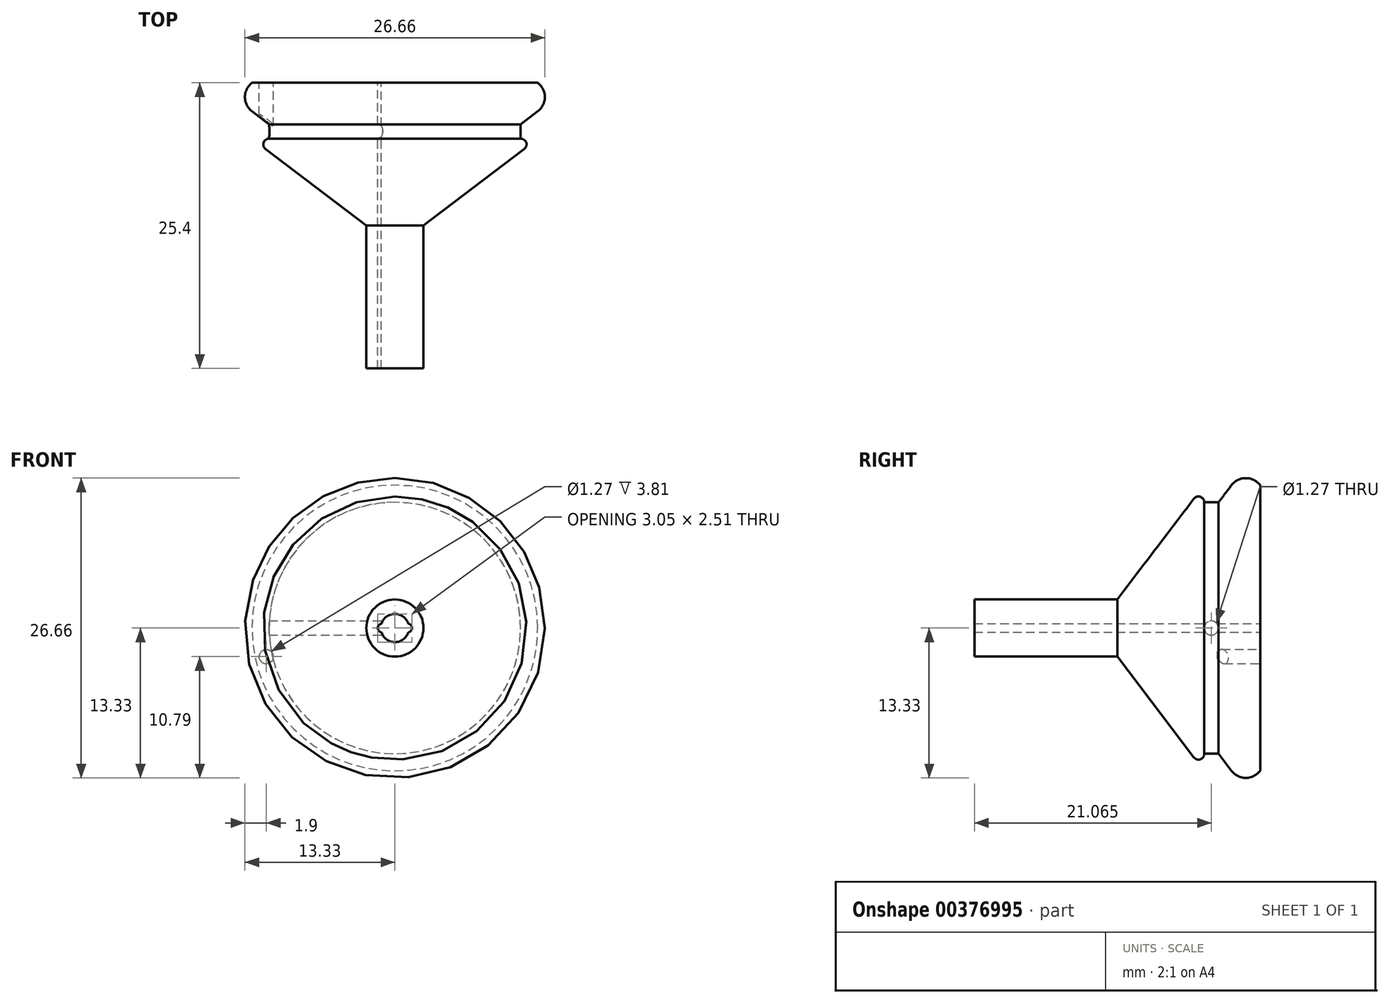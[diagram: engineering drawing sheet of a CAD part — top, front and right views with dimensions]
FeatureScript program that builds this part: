
annotation { "Feature Type Name" : "Feature", "Feature Type Description" : "" }
export const myFeature = defineFeature(function(context is Context, id is Id, definition is map)
    precondition{}
    {
        {
            var Q0;
            Q0=qCreatedBy(makeId("Right.planeOp"),FACE);
            var sketch = newSketch(context, id + "F0", { "sketchPlane" : qUnion([Q0])});
            skLineSegment(sketch, "E0", {"start": v(0, 1) * mm, "end": v(-25.4, 1) * mm});
            skLineSegment(sketch, "E1", {"start": v(-25.4, 1) * mm, "end": v(-25.4, 2.54) * mm});
            skLineSegment(sketch, "E2", {"start": v(-25.4, 2.54) * mm, "end": v(-12.7, 2.54) * mm});
            skLineSegment(sketch, "E3", {"start": v(-2.54, 12.7) * mm, "end": v(0, 12.7) * mm, "construction": true});
            skLineSegment(sketch, "E4", {"start": v(0, 12.7) * mm, "end": v(0, 1) * mm});
            skArc(sketch, "E5", {"start": v(0, 12.7) * mm, "mid": v(-1.27, 13.33) * mm, "end": v(-2.54, 12.7) * mm});
            skLineSegment(sketch, "E6", {"start": v(0, 0) * mm, "end": v(-25.4, 0) * mm, "construction": true});
            skLineSegment(sketch, "E7", {"start": v(-25.4, 0) * mm, "end": v(-25.4, 1) * mm, "construction": true});
            skLineSegment(sketch, "E8", {"start": v(-2.54, 12.7) * mm, "end": v(-3.7, 11.18) * mm});
            skLineSegment(sketch, "E9", {"start": v(-3.7, 11.18) * mm, "end": v(-4.97, 11.18) * mm});
            skLineSegment(sketch, "E10", {"start": v(-4.97, 11.18) * mm, "end": v(-4.97, 12.7) * mm});
            skLineSegment(sketch, "E11", {"start": v(-4.97, 12.7) * mm, "end": v(-12.7, 2.54) * mm});
            skLineSegment(sketch, "E12", {"start": v(-2.54, 12.7) * mm, "end": v(-4.97, 12.7) * mm, "construction": true});
            skSolve(sketch);
        }
        {
            var Q0;
            Q0 = qSketchRegion(id + "F0", true);
            var Q1;
            Q1=sQuery(id+"F0.wireOp",EDGE,"E6");
            revolve(context, id + "F1", {"entities" : qUnion([Q0]), "axis" : qUnion([Q1]), "revolveType" : RevolveType.FULL});
        }
        {
            var Q0;
            Q0=makeQuery(id+"F1.opRevolve","SWEPT_EDGE",EDGE,{"disambiguationData":[OSD([sQuery(id+"F0.wireOp",EDGE,"E10"),sQuery(id+"F0.wireOp",EDGE,"E11")])]});
            fillet(context, id + "F2", {"entities" : qUnion([Q0]), "radius" : 0.5 * mm, "tangentPropagation" : true, "allowEdgeOverflow" : false});
        }
        {
            var Q0;
            Q0=makeQuery(id+"F1.opRevolve","SWEPT_FACE",FACE,{"disambiguationData":[OSD([sQuery(id+"F0.wireOp",EDGE,"E4")])]});
            var sketch = newSketch(context, id + "F3", { "sketchPlane" : qUnion([Q0])});
            skLineSegment(sketch, "E13.bottom", {"start": v(-1.14, -0.13) * mm, "end": v(1.14, -0.13) * mm});
            skLineSegment(sketch, "E13.top", {"start": v(-1.14, 0.13) * mm, "end": v(1.14, 0.13) * mm});
            skLineSegment(sketch, "E13.left", {"start": v(-1.14, -0.13) * mm, "end": v(-1.14, 0.13) * mm, "construction": true});
            skLineSegment(sketch, "E13.right", {"start": v(1.14, -0.13) * mm, "end": v(1.14, 0.13) * mm, "construction": true});
            skPoint(sketch, "E13.middle", {"position": v(0, 0) * mm});
            skArc(sketch, "E14", {"start": v(-1.14, -0.13) * mm, "mid": v(-1.27, 0) * mm, "end": v(-1.14, 0.13) * mm});
            skArc(sketch, "E15", {"start": v(1.14, -0.13) * mm, "mid": v(1.27, 0) * mm, "end": v(1.14, 0.13) * mm});
            skSolve(sketch);
        }
        {
            var Q0;
            Q0 = qSketchRegion(id + "F3", true);
            extrude(context, id + "F4", {"entities" : qUnion([Q0]), "operationType" : NewBodyOperationType.REMOVE, "endBound" : BoundingType.THROUGH_ALL, "oppositeDirection" : true, "depth" : 25.4 * mm});
        }
        {
            var Q0;
            Q0=qCreatedBy(makeId("Right.planeOp"),FACE);
            var sketch = newSketch(context, id + "F5", { "sketchPlane" : qUnion([Q0])});
            skCircle(sketch, "E16", {"center": v(-4.33, 0) * mm, "radius": 0.64 * mm});
            skSolve(sketch);
        }
        {
            var Q0;
            Q0 = qSketchRegion(id + "F5", true);
            extrude(context, id + "F6", {"entities" : qUnion([Q0]), "operationType" : NewBodyOperationType.REMOVE, "endBound" : BoundingType.THROUGH_ALL, "oppositeDirection" : true, "depth" : 25.4 * mm});
        }
        {
            var Q0;
            Q0=makeQuery(id+"F1.opRevolve","SWEPT_FACE",FACE,{"disambiguationData":[OSD([sQuery(id+"F0.wireOp",EDGE,"E4")])]});
            var sketch = newSketch(context, id + "F7", { "sketchPlane" : qUnion([Q0])});
            skCircle(sketch, "E17", {"center": v(11.43, -2.54) * mm, "radius": 0.64 * mm});
            skSolve(sketch);
        }
        {
            var Q0;
            Q0 = qSketchRegion(id + "F7", true);
            extrude(context, id + "F8", {"entities" : qUnion([Q0]), "operationType" : NewBodyOperationType.REMOVE, "oppositeDirection" : true, "depth" : 3.8 * mm});
        }
        {
            var Q0;
            Q0=makeQuery(id+"F1.opRevolve","SWEPT_FACE",FACE,{"disambiguationData":[OSD([sQuery(id+"F0.wireOp",EDGE,"E4")])]});
            var sketch = newSketch(context, id + "F9", { "sketchPlane" : qUnion([Q0])});
            skArc(sketch, "E18.0", {"start": v(-1.2, -0.38) * mm, "mid": v(0, -1.25) * mm, "end": v(1.2, -0.38) * mm});
            skArc(sketch, "E18.1", {"start": v(-1.2, -0.38) * mm, "mid": v(-1.52, 0) * mm, "end": v(-1.2, 0.38) * mm});
            skArc(sketch, "E18.2", {"start": v(1.2, 0.38) * mm, "mid": v(0, 1.25) * mm, "end": v(-1.2, 0.38) * mm});
            skArc(sketch, "E18.3", {"start": v(1.2, -0.38) * mm, "mid": v(1.52, 0) * mm, "end": v(1.2, 0.38) * mm});
            skCircle(sketch, "E19.0", {"center": v(0, 0) * mm, "radius": 19.05 * mm});
            skSolve(sketch);
        }
        {
            var Q0;
            Q0=makeQuery(id+"F9.imprint","IMPRINT",FACE,{"disambiguationData":[TD([[makeQuery(id+"F9.imprint","IMPRINT",EDGE,{"derivedFrom":sQuery(id+"F9.wireOp",EDGE,"E18.0")}),1.0]])]});
            extrude(context, id + "F10", {"entities" : qUnion([Q0]), "operationType" : NewBodyOperationType.REMOVE, "endBound" : BoundingType.THROUGH_ALL, "oppositeDirection" : true, "depth" : 25.4 * mm});
        }
    });
